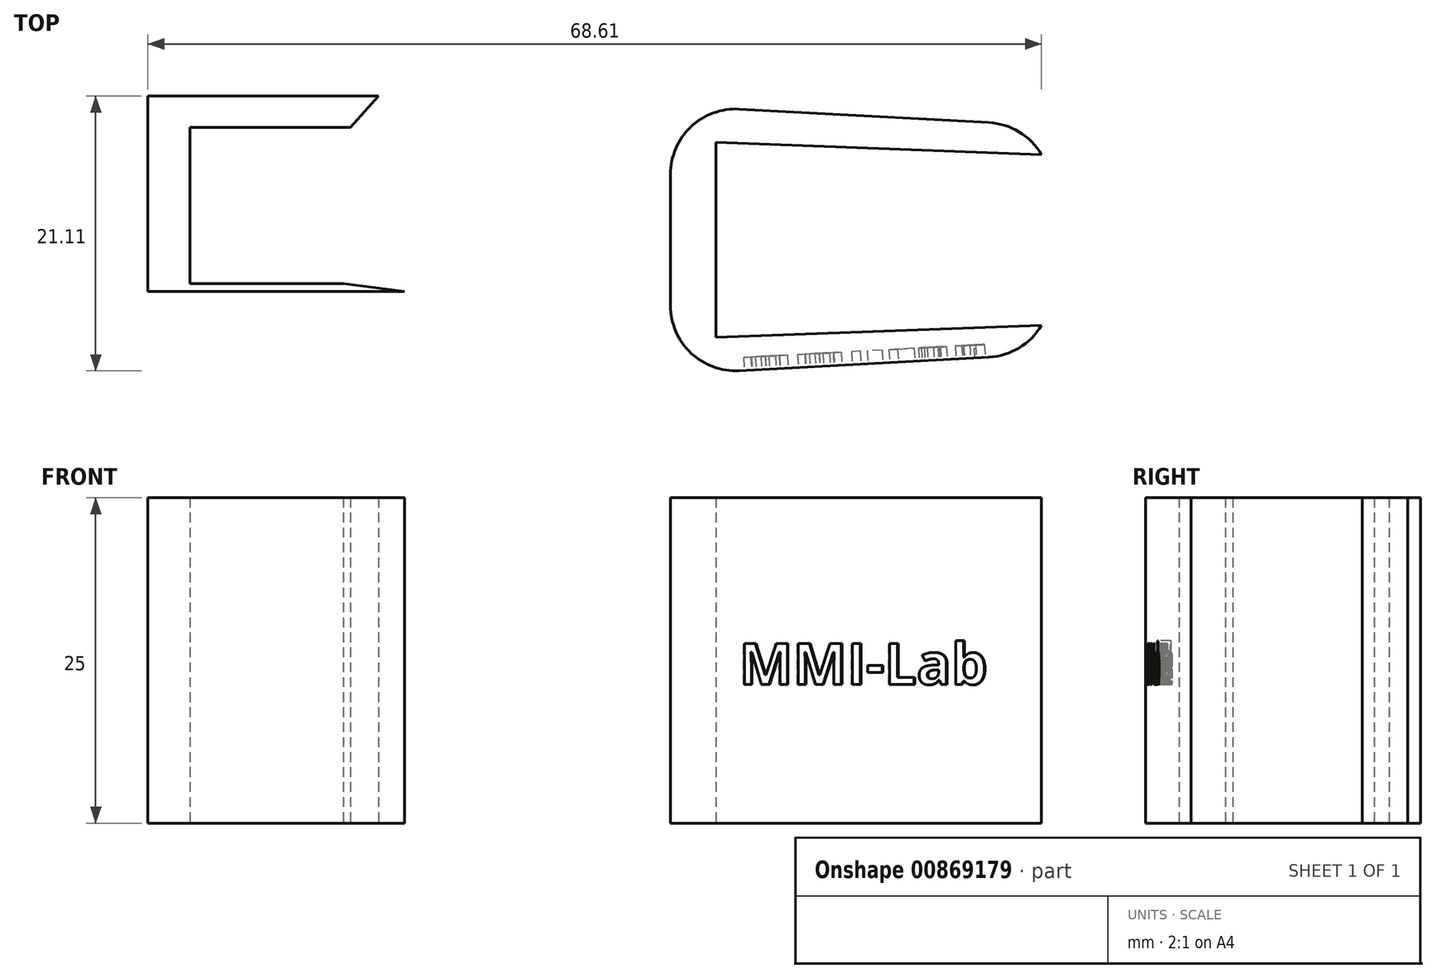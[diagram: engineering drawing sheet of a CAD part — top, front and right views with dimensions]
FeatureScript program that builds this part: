
annotation { "Feature Type Name" : "Feature", "Feature Type Description" : "" }
export const myFeature = defineFeature(function(context is Context, id is Id, definition is map)
    precondition{}
    {
        {
            var Q0;
            Q0=qCreatedBy(makeId("Top.planeOp"),FACE);
            var sketch = newSketch(context, id + "F0", { "sketchPlane" : qUnion([Q0])});
            skLineSegment(sketch, "E0", {"start": v(-12.12, 8.64) * mm, "end": v(-9.97, 11.05) * mm});
            skLineSegment(sketch, "E1", {"start": v(-9.97, 11.05) * mm, "end": v(-27.67, 11.05) * mm});
            skLineSegment(sketch, "E2", {"start": v(-27.67, 11.05) * mm, "end": v(-27.67, -3.95) * mm});
            skLineSegment(sketch, "E3", {"start": v(-27.67, -3.95) * mm, "end": v(-7.96, -3.95) * mm});
            skLineSegment(sketch, "E4", {"start": v(-7.96, -3.95) * mm, "end": v(-12.65, -3.36) * mm});
            skLineSegment(sketch, "E5", {"start": v(-12.65, -3.36) * mm, "end": v(-24.45, -3.36) * mm});
            skLineSegment(sketch, "E6", {"start": v(-24.45, -3.36) * mm, "end": v(-24.45, 8.64) * mm});
            skLineSegment(sketch, "E7", {"start": v(-24.45, 8.64) * mm, "end": v(-12.12, 8.64) * mm});
            skLineSegment(sketch, "E8", {"start": v(12.46, 0) * mm, "end": v(12.46, 10.33) * mm});
            skLineSegment(sketch, "E9", {"start": v(12.46, 10.33) * mm, "end": v(46.44, 8.5) * mm});
            skLineSegment(sketch, "E10", {"start": v(46.44, 8.5) * mm, "end": v(40.94, 6.56) * mm});
            skLineSegment(sketch, "E11", {"start": v(40.94, 6.56) * mm, "end": v(15.96, 7.5) * mm});
            skLineSegment(sketch, "E12", {"start": v(15.96, 7.5) * mm, "end": v(15.96, 0) * mm});
            skLineSegment(sketch, "E13.MirrorCS", {"start": v(12.46, 0) * mm, "end": v(12.46, -10.33) * mm});
            skLineSegment(sketch, "E14.MirrorCS", {"start": v(15.96, -7.5) * mm, "end": v(15.96, 0) * mm});
            skLineSegment(sketch, "E15.MirrorCS", {"start": v(40.94, -6.56) * mm, "end": v(15.96, -7.5) * mm});
            skLineSegment(sketch, "E16.MirrorCS", {"start": v(12.46, -10.33) * mm, "end": v(46.44, -8.5) * mm});
            skLineSegment(sketch, "E17.MirrorCS", {"start": v(46.44, -8.5) * mm, "end": v(40.94, -6.56) * mm});
            skSolve(sketch);
        }
        {
            var Q0;
            Q0 = qSketchRegion(id + "F0", true);
            extrude(context, id + "F1", {"entities" : qUnion([Q0]), "depth" : 25 * mm, "offsetDistance" : 25 * mm});
        }
        {
            var Q0;
            Q0=makeQuery(id+"F1.opExtrude","SWEPT_EDGE",EDGE,{"disambiguationData":[OSD([sQuery(id+"F0.wireOp",EDGE,"E8"),sQuery(id+"F0.wireOp",EDGE,"E9")])]});
            var Q1;
            Q1=makeQuery(id+"F1.opExtrude","SWEPT_EDGE",EDGE,{"disambiguationData":[OSD([sQuery(id+"F0.wireOp",EDGE,"E9"),sQuery(id+"F0.wireOp",EDGE,"E10")])]});
            var Q2;
            Q2=makeQuery(id+"F1.opExtrude","SWEPT_EDGE",EDGE,{"disambiguationData":[OSD([sQuery(id+"F0.wireOp",EDGE,"E16.MirrorCS"),sQuery(id+"F0.wireOp",EDGE,"E17.MirrorCS")])]});
            var Q3;
            Q3=makeQuery(id+"F1.opExtrude","SWEPT_EDGE",EDGE,{"disambiguationData":[OSD([sQuery(id+"F0.wireOp",EDGE,"E13.MirrorCS"),sQuery(id+"F0.wireOp",EDGE,"E16.MirrorCS")])]});
            fillet(context, id + "F2", {"entities" : qUnion([Q0, Q1, Q2, Q3]), "radius" : 5 * mm, "tangentPropagation" : true, "allowEdgeOverflow" : false});
        }
        {
            var Q0;
            Q0=makeQuery(id+"F1.opExtrude","SWEPT_FACE",FACE,{"disambiguationData":[OSD([sQuery(id+"F0.wireOp",EDGE,"E16.MirrorCS")])]});
            var sketch = newSketch(context, id + "F3", { "sketchPlane" : qUnion([Q0])});
            skText(sketch, "E18", { "text": "MMI-Lab", "fontName": "OpenSans-Bold.ttf"});
            const initialGuessF3  = {"E18": [0.01716, 0.01066, 1, 0, 0.00317]};
            skSetInitialGuess(sketch, initialGuessF3);
            skSolve(sketch);
        }
        {
            var Q0;
            Q0 = qSketchRegion(id + "F3", true);
            extrude(context, id + "F4", {"entities" : qUnion([Q0]), "depth" : -1 * mm, "offsetDistance" : 25 * mm});
        }
        {
            var Q0;
            Q0=makeQuery(id+"F4.opExtrude","SWEPT_BODY",BODY,{"disambiguationData":[OSD([sQuery(id+"F3.wireOp",EDGE,"E18.sketch_text.stroke-77"),sQuery(id+"F3.wireOp",EDGE,"E18.sketch_text.stroke-78"),sQuery(id+"F3.wireOp",EDGE,"E18.sketch_text.stroke-79"),sQuery(id+"F3.wireOp",EDGE,"E18.sketch_text.stroke-80"),sQuery(id+"F3.wireOp",EDGE,"E18.sketch_text.stroke-81"),sQuery(id+"F3.wireOp",EDGE,"E18.sketch_text.stroke-82"),sQuery(id+"F3.wireOp",EDGE,"E18.sketch_text.stroke-83"),sQuery(id+"F3.wireOp",EDGE,"E18.sketch_text.stroke-84"),sQuery(id+"F3.wireOp",EDGE,"E18.sketch_text.stroke-85"),sQuery(id+"F3.wireOp",EDGE,"E18.sketch_text.stroke-86"),sQuery(id+"F3.wireOp",EDGE,"E18.sketch_text.stroke-87"),sQuery(id+"F3.wireOp",EDGE,"E18.sketch_text.stroke-88"),sQuery(id+"F3.wireOp",EDGE,"E18.sketch_text.stroke-89"),sQuery(id+"F3.wireOp",EDGE,"E18.sketch_text.stroke-90"),sQuery(id+"F3.wireOp",EDGE,"E18.sketch_text.stroke-91"),sQuery(id+"F3.wireOp",EDGE,"E18.sketch_text.stroke-92"),sQuery(id+"F3.wireOp",EDGE,"E18.sketch_text.stroke-93"),sQuery(id+"F3.wireOp",EDGE,"E18.sketch_text.stroke-94"),sQuery(id+"F3.wireOp",EDGE,"E18.sketch_text.stroke-95"),sQuery(id+"F3.wireOp",EDGE,"E18.sketch_text.stroke-96"),sQuery(id+"F3.wireOp",EDGE,"E18.sketch_text.stroke-97"),sQuery(id+"F3.wireOp",EDGE,"E18.sketch_text.stroke-98"),sQuery(id+"F3.wireOp",EDGE,"E18.sketch_text.stroke-99")])]});
            var Q1;
            Q1=makeQuery(id+"F4.opExtrude","SWEPT_BODY",BODY,{"disambiguationData":[OSD([sQuery(id+"F3.wireOp",EDGE,"E18.sketch_text.stroke-52"),sQuery(id+"F3.wireOp",EDGE,"E18.sketch_text.stroke-53"),sQuery(id+"F3.wireOp",EDGE,"E18.sketch_text.stroke-54"),sQuery(id+"F3.wireOp",EDGE,"E18.sketch_text.stroke-55"),sQuery(id+"F3.wireOp",EDGE,"E18.sketch_text.stroke-56"),sQuery(id+"F3.wireOp",EDGE,"E18.sketch_text.stroke-57"),sQuery(id+"F3.wireOp",EDGE,"E18.sketch_text.stroke-58"),sQuery(id+"F3.wireOp",EDGE,"E18.sketch_text.stroke-59"),sQuery(id+"F3.wireOp",EDGE,"E18.sketch_text.stroke-60"),sQuery(id+"F3.wireOp",EDGE,"E18.sketch_text.stroke-61"),sQuery(id+"F3.wireOp",EDGE,"E18.sketch_text.stroke-62"),sQuery(id+"F3.wireOp",EDGE,"E18.sketch_text.stroke-63"),sQuery(id+"F3.wireOp",EDGE,"E18.sketch_text.stroke-64"),sQuery(id+"F3.wireOp",EDGE,"E18.sketch_text.stroke-65"),sQuery(id+"F3.wireOp",EDGE,"E18.sketch_text.stroke-66"),sQuery(id+"F3.wireOp",EDGE,"E18.sketch_text.stroke-67"),sQuery(id+"F3.wireOp",EDGE,"E18.sketch_text.stroke-68"),sQuery(id+"F3.wireOp",EDGE,"E18.sketch_text.stroke-69"),sQuery(id+"F3.wireOp",EDGE,"E18.sketch_text.stroke-70"),sQuery(id+"F3.wireOp",EDGE,"E18.sketch_text.stroke-71"),sQuery(id+"F3.wireOp",EDGE,"E18.sketch_text.stroke-72"),sQuery(id+"F3.wireOp",EDGE,"E18.sketch_text.stroke-73"),sQuery(id+"F3.wireOp",EDGE,"E18.sketch_text.stroke-74"),sQuery(id+"F3.wireOp",EDGE,"E18.sketch_text.stroke-75"),sQuery(id+"F3.wireOp",EDGE,"E18.sketch_text.stroke-76")])]});
            var Q2;
            Q2=makeQuery(id+"F4.opExtrude","SWEPT_BODY",BODY,{"disambiguationData":[OSD([sQuery(id+"F3.wireOp",EDGE,"E18.sketch_text.stroke-46"),sQuery(id+"F3.wireOp",EDGE,"E18.sketch_text.stroke-47"),sQuery(id+"F3.wireOp",EDGE,"E18.sketch_text.stroke-48"),sQuery(id+"F3.wireOp",EDGE,"E18.sketch_text.stroke-49"),sQuery(id+"F3.wireOp",EDGE,"E18.sketch_text.stroke-50"),sQuery(id+"F3.wireOp",EDGE,"E18.sketch_text.stroke-51")])]});
            var Q3;
            Q3=makeQuery(id+"F4.opExtrude","SWEPT_BODY",BODY,{"disambiguationData":[OSD([sQuery(id+"F3.wireOp",EDGE,"E18.sketch_text.stroke-42"),sQuery(id+"F3.wireOp",EDGE,"E18.sketch_text.stroke-43"),sQuery(id+"F3.wireOp",EDGE,"E18.sketch_text.stroke-44"),sQuery(id+"F3.wireOp",EDGE,"E18.sketch_text.stroke-45")])]});
            var Q4;
            Q4=makeQuery(id+"F4.opExtrude","SWEPT_BODY",BODY,{"disambiguationData":[OSD([sQuery(id+"F3.wireOp",EDGE,"E18.sketch_text.stroke-38"),sQuery(id+"F3.wireOp",EDGE,"E18.sketch_text.stroke-39"),sQuery(id+"F3.wireOp",EDGE,"E18.sketch_text.stroke-40"),sQuery(id+"F3.wireOp",EDGE,"E18.sketch_text.stroke-41")])]});
            var Q5;
            Q5=makeQuery(id+"F4.opExtrude","SWEPT_BODY",BODY,{"disambiguationData":[OSD([sQuery(id+"F3.wireOp",EDGE,"E18.sketch_text.stroke-0"),sQuery(id+"F3.wireOp",EDGE,"E18.sketch_text.stroke-1"),sQuery(id+"F3.wireOp",EDGE,"E18.sketch_text.stroke-2"),sQuery(id+"F3.wireOp",EDGE,"E18.sketch_text.stroke-3"),sQuery(id+"F3.wireOp",EDGE,"E18.sketch_text.stroke-4"),sQuery(id+"F3.wireOp",EDGE,"E18.sketch_text.stroke-5"),sQuery(id+"F3.wireOp",EDGE,"E18.sketch_text.stroke-6"),sQuery(id+"F3.wireOp",EDGE,"E18.sketch_text.stroke-7"),sQuery(id+"F3.wireOp",EDGE,"E18.sketch_text.stroke-8"),sQuery(id+"F3.wireOp",EDGE,"E18.sketch_text.stroke-9"),sQuery(id+"F3.wireOp",EDGE,"E18.sketch_text.stroke-10"),sQuery(id+"F3.wireOp",EDGE,"E18.sketch_text.stroke-11"),sQuery(id+"F3.wireOp",EDGE,"E18.sketch_text.stroke-12"),sQuery(id+"F3.wireOp",EDGE,"E18.sketch_text.stroke-13"),sQuery(id+"F3.wireOp",EDGE,"E18.sketch_text.stroke-14"),sQuery(id+"F3.wireOp",EDGE,"E18.sketch_text.stroke-15"),sQuery(id+"F3.wireOp",EDGE,"E18.sketch_text.stroke-16"),sQuery(id+"F3.wireOp",EDGE,"E18.sketch_text.stroke-17"),sQuery(id+"F3.wireOp",EDGE,"E18.sketch_text.stroke-18")])]});
            var Q6;
            Q6=makeQuery(id+"F4.opExtrude","SWEPT_BODY",BODY,{"disambiguationData":[OSD([sQuery(id+"F3.wireOp",EDGE,"E18.sketch_text.stroke-19"),sQuery(id+"F3.wireOp",EDGE,"E18.sketch_text.stroke-20"),sQuery(id+"F3.wireOp",EDGE,"E18.sketch_text.stroke-21"),sQuery(id+"F3.wireOp",EDGE,"E18.sketch_text.stroke-22"),sQuery(id+"F3.wireOp",EDGE,"E18.sketch_text.stroke-23"),sQuery(id+"F3.wireOp",EDGE,"E18.sketch_text.stroke-24"),sQuery(id+"F3.wireOp",EDGE,"E18.sketch_text.stroke-25"),sQuery(id+"F3.wireOp",EDGE,"E18.sketch_text.stroke-26"),sQuery(id+"F3.wireOp",EDGE,"E18.sketch_text.stroke-27"),sQuery(id+"F3.wireOp",EDGE,"E18.sketch_text.stroke-28"),sQuery(id+"F3.wireOp",EDGE,"E18.sketch_text.stroke-29"),sQuery(id+"F3.wireOp",EDGE,"E18.sketch_text.stroke-30"),sQuery(id+"F3.wireOp",EDGE,"E18.sketch_text.stroke-31"),sQuery(id+"F3.wireOp",EDGE,"E18.sketch_text.stroke-32"),sQuery(id+"F3.wireOp",EDGE,"E18.sketch_text.stroke-33"),sQuery(id+"F3.wireOp",EDGE,"E18.sketch_text.stroke-34"),sQuery(id+"F3.wireOp",EDGE,"E18.sketch_text.stroke-35"),sQuery(id+"F3.wireOp",EDGE,"E18.sketch_text.stroke-36"),sQuery(id+"F3.wireOp",EDGE,"E18.sketch_text.stroke-37")])]});
            var Q7;
            Q7=makeQuery(id+"F1.opExtrude","SWEPT_BODY",BODY,{"disambiguationData":[OSD([sQuery(id+"F0.wireOp",EDGE,"E8"),sQuery(id+"F0.wireOp",EDGE,"E9"),sQuery(id+"F0.wireOp",EDGE,"E10"),sQuery(id+"F0.wireOp",EDGE,"E11"),sQuery(id+"F0.wireOp",EDGE,"E12"),sQuery(id+"F0.wireOp",EDGE,"E13.MirrorCS"),sQuery(id+"F0.wireOp",EDGE,"E14.MirrorCS"),sQuery(id+"F0.wireOp",EDGE,"E15.MirrorCS"),sQuery(id+"F0.wireOp",EDGE,"E16.MirrorCS"),sQuery(id+"F0.wireOp",EDGE,"E17.MirrorCS")])]});
            booleanBodies(context, id + "F5", {"operationType" : BooleanOperationType.SUBTRACTION, "tools" : qUnion([Q0, Q1, Q2, Q3, Q4, Q5, Q6]), "targets" : qUnion([Q7])});
        }
    });
